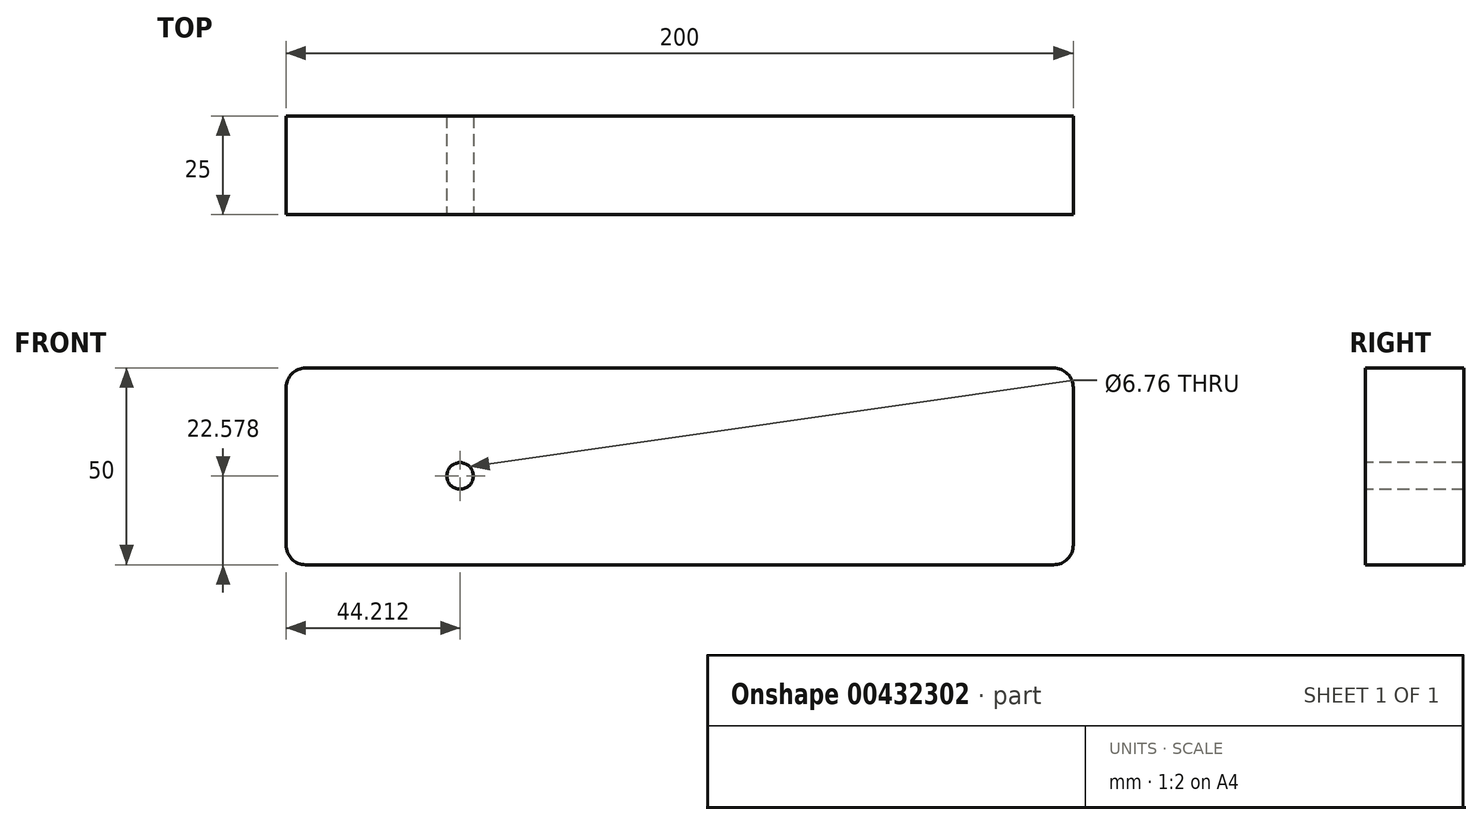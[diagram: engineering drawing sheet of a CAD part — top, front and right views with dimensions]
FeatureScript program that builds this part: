
annotation { "Feature Type Name" : "Feature", "Feature Type Description" : "" }
export const myFeature = defineFeature(function(context is Context, id is Id, definition is map)
    precondition{}
    {
        {
            var Q0;
            Q0=qCreatedBy(makeId("Front.planeOp"),FACE);
            var sketch = newSketch(context, id + "F0", { "sketchPlane" : qUnion([Q0])});
            skLineSegment(sketch, "E0.bottom", {"start": v(-100, 18.33) * mm, "end": v(100, 18.33) * mm});
            skLineSegment(sketch, "E0.top", {"start": v(-100, -31.67) * mm, "end": v(100, -31.67) * mm});
            skLineSegment(sketch, "E0.left", {"start": v(-100, 18.33) * mm, "end": v(-100, -31.67) * mm});
            skLineSegment(sketch, "E0.right", {"start": v(100, 18.33) * mm, "end": v(100, -31.67) * mm});
            skPoint(sketch, "E0.middle", {"position": v(0, -6.67) * mm});
            skSolve(sketch);
        }
        {
            var Q0;
            Q0=makeQuery(id+"F0.imprint","IMPRINT",FACE,{"disambiguationData":[TD([[makeQuery(id+"F0.imprint","IMPRINT",EDGE,{"derivedFrom":sQuery(id+"F0.wireOp",EDGE,"E0.bottom")}),-1.0]])]});
            extrude(context, id + "F1", {"entities" : qUnion([Q0]), "depth" : 25 * mm});
        }
        {
            var Q0;
            Q0=makeQuery(id+"F1.opExtrude","SWEPT_EDGE",EDGE,{"disambiguationData":[OSD([sQuery(id+"F0.wireOp",EDGE,"E0.bottom"),sQuery(id+"F0.wireOp",EDGE,"E0.left")])]});
            var Q1;
            Q1=makeQuery(id+"F1.opExtrude","SWEPT_EDGE",EDGE,{"disambiguationData":[OSD([sQuery(id+"F0.wireOp",EDGE,"E0.bottom"),sQuery(id+"F0.wireOp",EDGE,"E0.right")])]});
            var Q2;
            Q2=makeQuery(id+"F1.opExtrude","SWEPT_EDGE",EDGE,{"disambiguationData":[OSD([sQuery(id+"F0.wireOp",EDGE,"E0.top"),sQuery(id+"F0.wireOp",EDGE,"E0.right")])]});
            var Q3;
            Q3=makeQuery(id+"F1.opExtrude","SWEPT_EDGE",EDGE,{"disambiguationData":[OSD([sQuery(id+"F0.wireOp",EDGE,"E0.top"),sQuery(id+"F0.wireOp",EDGE,"E0.left")])]});
            fillet(context, id + "F2", {"entities" : qUnion([Q0, Q1, Q2, Q3]), "radius" : 5 * mm, "tangentPropagation" : true, "allowEdgeOverflow" : false});
        }
        {
            var Q0;
            Q0=makeQuery(id+"F1.opExtrude","CAP_FACE",FACE,{"disambiguationData":[OSD([sQuery(id+"F0.wireOp",EDGE,"E0.bottom"),sQuery(id+"F0.wireOp",EDGE,"E0.top"),sQuery(id+"F0.wireOp",EDGE,"E0.left"),sQuery(id+"F0.wireOp",EDGE,"E0.right")])],"isStart":false});
            var sketch = newSketch(context, id + "F3", { "sketchPlane" : qUnion([Q0])});
            skPoint(sketch, "E1", {"position": v(-43.15, 0) * mm});
            skSolve(sketch);
        }
        {
            var Q0;
            {var subQ3=sQuery(id+"F0.wireOp",EDGE,"E0.bottom");Q0=makeQuery(id+"F3.imprint","IMPRINT",FACE,{"disambiguationData":[TD([[makeQuery(id+"F3.imprint","IMPRINT",EDGE,{"derivedFrom":makeQuery(id+"F1.opExtrude","CAP_EDGE",EDGE,{"disambiguationData":[OSD([subQ3])],"isStart":false})}),-1.0]])]});}
            var sketch = newSketch(context, id + "F4", { "sketchPlane" : qUnion([Q0])});
            skPoint(sketch, "E2", {"position": v(-55.79, -9.1) * mm});
            skCircle(sketch, "E3", {"center": v(-55.79, -9.1) * mm, "radius": 7.8 * mm});
            skSolve(sketch);
        }
        {
            var Q0;
            Q0=sQuery(id+"F4.wireOp",VERTEX,"E2");
            var Q1;
            Q1=makeQuery(id+"F1.opExtrude","SWEPT_BODY",BODY,{"disambiguationData":[OSD([sQuery(id+"F0.wireOp",EDGE,"E0.bottom"),sQuery(id+"F0.wireOp",EDGE,"E0.top"),sQuery(id+"F0.wireOp",EDGE,"E0.left"),sQuery(id+"F0.wireOp",EDGE,"E0.right")])]});
            hole(context, id + "F5", {"style" : HoleStyle.SIMPLE, "endStyle" : HoleEndStyle.THROUGH, "standardTappedOrClearance" : lookupTablePath({ "standard" : "ANSI", "fit" : "Normal (ASME)", "size" : "1/4", "type" : "Clearance" }), "standardBlindInLast" : lookupTablePath({ "fit" : "Free", "standard" : "ANSI", "size" : "1/4", "type" : "Clearance" }), "holeDiameter" : 6.76 * mm, "isTappedThrough" : true, "tappedDepth" : 12 * mm, "tapClearance" : 3, "locations" : qUnion([Q0]), "scope" : qUnion([Q1])});
        }
    });
